# Revit family: Emergency_Equipment-Tepid-Wall_Mounted_Eye_Face_Wash-T2535
name_source: partatom
category: Plumbing Fixtures
revit_build: Autodesk Revit Architecture 2016 (Build: 20150220_1215(x64)
units: mm (PartAtom-declared; Revit-internal decimal feet)

## family parameters
Always vertical = No
Cut with Voids When Loaded = No
OmniClass Number = 23.45.05.14.24
OmniClass Title = Eye Wash Fountains
Part Type = Normal
Room Calculation Point = No
Round Connector Dimension = Use Diameter
Shared = No
Work Plane-Based = Yes

## types (4) — shared parameters
C Pipe = 2.56 "
CW Connection = Yes
Cold Water Connection = 1"
Default Elevation = 48 "
Description = Wall Mounted Eye-Face Wash
Dimension Disclaimer = Dimensions are ±0.50”. Design and specifications are subject to change without notice.
Drain Connection = 1"
HW Connection = Yes
Height = 10.5 "
Hot Water Connection = 1"
Length = 30.7 "
Length offset = 9.39 "
Manufacturer = Stingray Systems
Mount Height = 27 "
Product Documentation Link = http://www.tepid.com
Product Name = Wall Mounted Barrier-Free Eye-Face Wash
Product Page URL = http://www.tepid.com
URL = www.tepid.com
Vent Connection = No
Version = 2016-v1.0a
Waste Connection = Yes

## per-type parameters (varying)
| type | AB | Bowl Material | Filter | Width | nab |
| T2535-NFT-ABNA | Yes | Plastic - Stingray - ABS AB | No | 16.3 " | No |
| T2535-NFT-SSNA | No | Metal - Stingray - Stainless Steel SS | No | 14.3 " | Yes |
| T2535-FLT-SSNA | No | Metal - Stingray - Stainless Steel SS | Yes | 14.3 " | Yes |
| T2535-FLT-ABNA | Yes | Plastic - Stingray - ABS AB | Yes | 16.3 " | No |

note: column(s) folded — value = type name in every type: Model

## geometry (parser evidence)
native form markers: Sweep x6
no freeform markers — native parametric forms only
